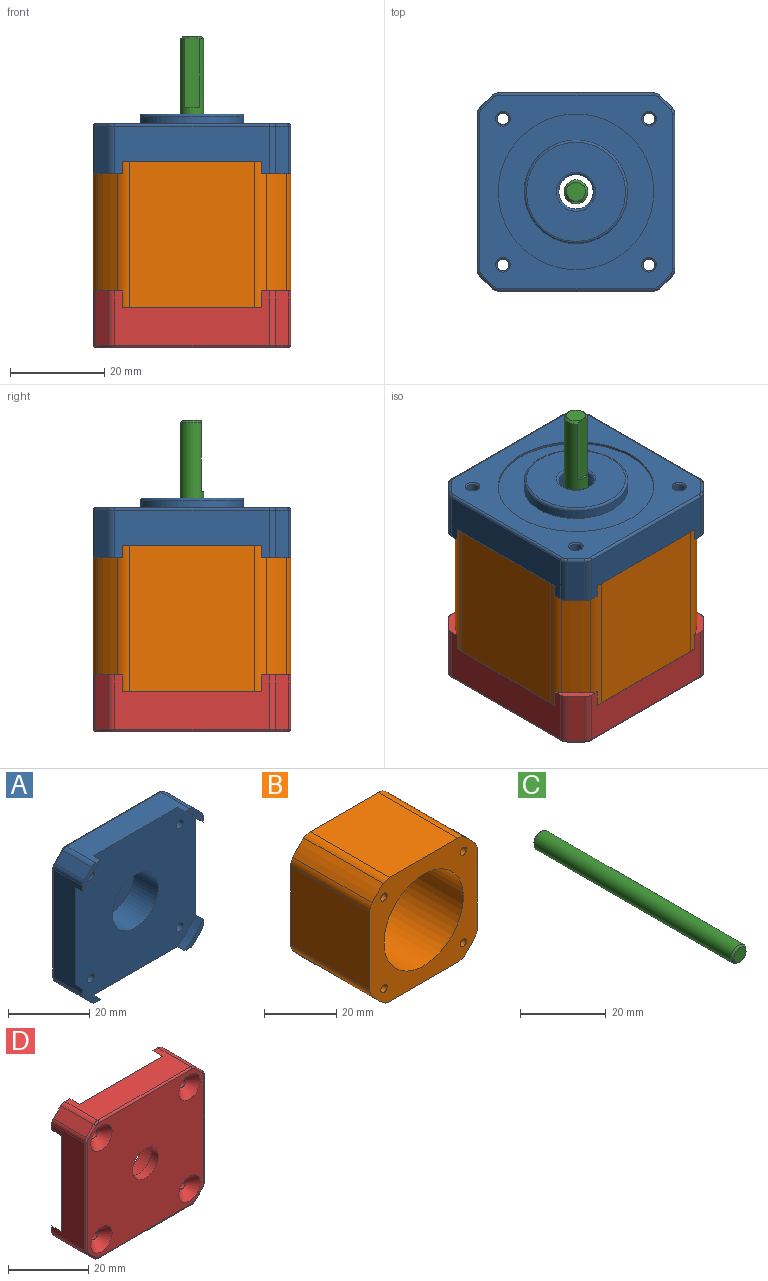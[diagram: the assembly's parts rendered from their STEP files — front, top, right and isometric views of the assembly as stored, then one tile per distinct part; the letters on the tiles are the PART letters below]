
ASSEMBLY  parts=4 mates=3
PART A: 59 faces, bbox 42.3x12.6x42.3 mm
  f0: cylinder r=3.65mm len=7.3mm, axis (0,-1,0), area 20.6mm2, adj f28,f53
  f1: plane 42x42mm, normal (0,-1,0), area 1472mm2, adj f2,f4,f6,f8,f9,f10,f11,f14
  f2: plane 32.74x10.1mm, normal (0,0,1), area 254.6mm2, adj f1,f19,f20,f21,f22,f30,f31,f51
  f3: plane 10.1x2.63mm, normal (0.71,0,0.71), area 37.5mm2, adj f22,f29,f30,f47
  f4: plane 32.74x10.1mm, normal (1,0,0), area 254.6mm2, adj f1,f21,f22,f25,f26,f29,f36,f43
  f5: plane 10.1x2.63mm, normal (0.71,0,-0.71), area 37.5mm2, adj f26,f35,f36,f39
  f6: plane 32.74x10.1mm, normal (0,0,-1), area 254.6mm2, adj f1,f23,f24,f25,f26,f34,f35,f38
  f7: plane 10.1x2.63mm, normal (-0.71,0,-0.71), area 37.5mm2, adj f24,f33,f34,f42
  f8: plane 32.74x10.1mm, normal (-1,0,0), area 254.6mm2, adj f1,f19,f20,f23,f24,f32,f33,f46
  f9: cylinder r=1.25mm len=7.7mm, axis (0,-1,0), area 60.5mm2, adj f1,f58
  f10: cylinder r=1.25mm len=7.7mm, axis (0,-1,0), area 60.5mm2, adj f1,f57
  f11: cylinder r=1.25mm len=7.7mm, axis (0,-1,0), area 60.5mm2, adj f1,f56
  f12: plane 10.1x2.63mm, normal (-0.71,0,0.71), area 37.5mm2, adj f20,f31,f32,f50
  f13: cylinder r=16.5mm len=33mm, axis (0,-1,0), area 51.8mm2, adj f15,f16
  f14: cylinder r=1.25mm len=7.7mm, axis (0,-1,0), area 60.5mm2, adj f1,f55
  f15: plane 41x41mm, normal (0,1,0), area 770.5mm2, adj f13,f37,f38,f39,f40,f41,f42,f43
  f16: plane 33x33mm, normal (0,1,0), area 475.2mm2, adj f13,f17
  f17: cylinder r=11mm len=22mm, axis (0,-1,0), area 138.2mm2, adj f16,f54
  f18: plane 21x21mm, normal (0,1,0), area 292.3mm2, adj f53,f54
  f19: cylinder r=25.6mm len=6.36mm, axis (0,1,0), area 23.5mm2, adj f1,f2,f8,f20
  f20: plane 6.36x6.36mm, normal (0,-1,0), area 10.4mm2, adj f2,f8,f12,f19,f31,f32
  f21: cylinder r=25.6mm len=6.36mm, axis (0,1,0), area 23.5mm2, adj f1,f2,f4,f22
  f22: plane 6.36x6.36mm, normal (0,-1,0), area 10.4mm2, adj f2,f3,f4,f21,f29,f30
  f23: cylinder r=25.6mm len=6.36mm, axis (0,1,0), area 23.5mm2, adj f1,f6,f8,f24
  f24: plane 6.36x6.36mm, normal (0,-1,0), area 10.4mm2, adj f6,f7,f8,f23,f33,f34
  f25: cylinder r=25.6mm len=6.36mm, axis (0,1,0), area 23.5mm2, adj f1,f4,f6,f26
  f26: plane 6.36x6.36mm, normal (0,-1,0), area 10.4mm2, adj f4,f5,f6,f25,f35,f36
  f27: cylinder r=8mm len=16mm, axis (0,-1,0), area 432.3mm2, adj f1,f28
  f28: plane 16x16mm, normal (0,-1,0), area 159.2mm2, adj f0,f27
  f29: cylinder r=2mm len=10.1mm, axis (0,-1,0), area 15.9mm2, adj f3,f4,f22,f45
  f30: cylinder r=2mm len=10.1mm, axis (0,-1,0), area 15.9mm2, adj f2,f3,f22,f49
  f31: cylinder r=2mm len=10.1mm, axis (0,-1,0), area 15.9mm2, adj f2,f12,f20,f52
  f32: cylinder r=2mm len=10.1mm, axis (0,1,0), area 15.9mm2, adj f8,f12,f20,f48
  f33: cylinder r=2mm len=10.1mm, axis (0,-1,0), area 15.9mm2, adj f7,f8,f24,f44
  f34: cylinder r=2mm len=10.1mm, axis (0,-1,0), area 15.9mm2, adj f6,f7,f24,f40
  f35: cylinder r=2mm len=10.1mm, axis (0,-1,0), area 15.9mm2, adj f5,f6,f26,f37
  f36: cylinder r=2mm len=10.1mm, axis (0,1,0), area 15.9mm2, adj f4,f5,f26,f41
  f37: torus R=1.5mm, axis (0,1,0), area 1.1mm2, adj f15,f35,f38,f39
  f38: cylinder r=0.5mm len=32.74mm, axis (1,0,0), area 25.7mm2, adj f6,f15,f37,f40
  f39: cylinder r=0.5mm len=2.98mm, axis (0.71,0,0.71), area 2.9mm2, adj f5,f15,f37,f41
  f40: torus R=1.5mm, axis (0,1,0), area 1.1mm2, adj f15,f34,f38,f42
  f41: torus R=1.5mm, axis (0,1,0), area 1.1mm2, adj f15,f36,f39,f43
  f42: cylinder r=0.5mm len=2.98mm, axis (0.71,0,-0.71), area 2.9mm2, adj f7,f15,f40,f44
  f43: cylinder r=0.5mm len=32.74mm, axis (0,0,1), area 25.7mm2, adj f4,f15,f41,f45
  f44: torus R=1.5mm, axis (0,1,0), area 1.1mm2, adj f15,f33,f42,f46
  f45: torus R=1.5mm, axis (0,1,0), area 1.1mm2, adj f15,f29,f43,f47
  f46: cylinder r=0.5mm len=32.74mm, axis (0,0,-1), area 25.7mm2, adj f8,f15,f44,f48
  f47: cylinder r=0.5mm len=2.98mm, axis (-0.71,0,0.71), area 2.9mm2, adj f3,f15,f45,f49
  f48: torus R=1.5mm, axis (0,1,0), area 1.1mm2, adj f15,f32,f46,f50
  f49: torus R=1.5mm, axis (0,1,0), area 1.1mm2, adj f15,f30,f47,f51
  f50: cylinder r=0.5mm len=2.98mm, axis (-0.71,0,-0.71), area 2.9mm2, adj f12,f15,f48,f52
  f51: cylinder r=0.5mm len=32.74mm, axis (-1,0,0), area 25.7mm2, adj f2,f15,f49,f52
  f52: torus R=1.5mm, axis (0,1,0), area 1.1mm2, adj f15,f31,f50,f51
  f53: torus R=4.15mm, axis (0,1,0), area 18.9mm2, adj f0,f18
  f54: torus R=10.5mm, axis (0,1,0), area 53.4mm2, adj f17,f18
  f55: cone r=1.25mm half-angle=45deg, axis (0,1,0), area 3.7mm2, adj f14,f15
  f56: cone r=1.25mm half-angle=45deg, axis (0,1,0), area 3.7mm2, adj f11,f15
  f57: cone r=1.25mm half-angle=45deg, axis (0,1,0), area 3.7mm2, adj f10,f15
  f58: cone r=1.25mm half-angle=45deg, axis (0,1,0), area 3.7mm2, adj f9,f15
PART B: 23 faces, bbox 42x31x42 mm
  f0: plane 42x42mm, normal (0,1,0), area 916.8mm2, adj f1,f2,f3,f4,f5,f6,f7,f8
  f1: cylinder r=25.6mm len=31mm, axis (0,-1,0), area 191.4mm2, adj f0,f16,f17,f22
  f2: plane 31x26.65mm, normal (0,0,-1), area 826.2mm2, adj f0,f15,f16,f22
  f3: cylinder r=25.6mm len=31mm, axis (0,-1,0), area 191.4mm2, adj f0,f14,f15,f22
  f4: plane 31x26.65mm, normal (-1,0,0), area 826.2mm2, adj f0,f14,f21,f22
  f5: cylinder r=25.6mm len=31mm, axis (0,-1,0), area 191.4mm2, adj f0,f20,f21,f22
  f6: plane 31x26.65mm, normal (0,0,1), area 826.2mm2, adj f0,f19,f20,f22
  f7: cylinder r=25.6mm len=31mm, axis (0,-1,0), area 191.4mm2, adj f0,f18,f19,f22
  f8: plane 31x26.65mm, normal (1,0,0), area 826.2mm2, adj f0,f17,f18,f22
  f9: cylinder r=15.5mm len=31mm, axis (0,-1,0), area 3019.1mm2, adj f0,f22
  f10: cylinder r=1.25mm len=31mm, axis (0,-1,0), area 243.5mm2, adj f0,f22
  f11: cylinder r=1.25mm len=31mm, axis (0,-1,0), area 243.5mm2, adj f0,f22
  f12: cylinder r=1.25mm len=31mm, axis (0,-1,0), area 243.5mm2, adj f0,f22
  f13: cylinder r=1.25mm len=31mm, axis (0,-1,0), area 243.5mm2, adj f0,f22
  f14: cylinder r=4mm len=31mm, axis (0,-1,0), area 82.4mm2, adj f0,f3,f4,f22
  f15: cylinder r=4mm len=31mm, axis (0,-1,0), area 82.4mm2, adj f0,f2,f3,f22
  f16: cylinder r=4mm len=31mm, axis (0,-1,0), area 82.4mm2, adj f0,f1,f2,f22
  f17: cylinder r=4mm len=31mm, axis (0,-1,0), area 82.4mm2, adj f0,f1,f8,f22
  f18: cylinder r=4mm len=31mm, axis (0,-1,0), area 82.4mm2, adj f0,f7,f8,f22
  f19: cylinder r=4mm len=31mm, axis (0,-1,0), area 82.4mm2, adj f0,f6,f7,f22
  f20: cylinder r=4mm len=31mm, axis (0,-1,0), area 82.4mm2, adj f0,f5,f6,f22
  f21: cylinder r=4mm len=31mm, axis (0,-1,0), area 82.4mm2, adj f0,f4,f5,f22
  f22: plane 42x42mm, normal (0,-1,0), area 916.8mm2, adj f1,f2,f3,f4,f5,f6,f7,f8
PART C: 7 faces, bbox 5x66x5 mm
  f0: cylinder r=2.5mm len=65mm, axis (0,-1,0), area 974.4mm2, adj f2,f3,f4,f6
  f1: plane 4x4mm, normal (0,1,0), area 12.6mm2, adj f4
  f2: plane 15x3mm, normal (0,0,-1), area 44.5mm2, adj f0,f3,f4
  f3: plane 3x0.5mm, normal (0,1,0), area 1mm2, adj f0,f2
  f4: cone r=2mm half-angle=45deg, axis (0,-1,0), area 8.6mm2, adj f0,f1,f2
  f5: plane 4x4mm, normal (0,-1,0), area 12.6mm2, adj f6
  f6: cone r=2.5mm half-angle=45deg, axis (0,1,0), area 10mm2, adj f0,f5
PART D: 53 faces, bbox 42.3x12x42.3 mm
  f0: cylinder r=4.5mm len=9mm, axis (0,-1,0), area 70.7mm2, adj f10,f28
  f1: plane 32.74x11.5mm, normal (0,0,1), area 274.1mm2, adj f9,f11,f13,f14,f16,f30,f31,f50
  f2: plane 32.74x11.5mm, normal (1,0,0), area 274.1mm2, adj f9,f11,f13,f20,f22,f29,f36,f42
  f3: plane 32.74x11.5mm, normal (0,0,-1), area 274.1mm2, adj f9,f17,f19,f20,f22,f34,f35,f39
  f4: plane 32.74x11.5mm, normal (-1,0,0), area 274.1mm2, adj f9,f14,f16,f17,f19,f32,f33,f47
  f5: cylinder r=1.25mm len=6mm, axis (0,-1,0), area 47.1mm2, adj f9,f26
  f6: cylinder r=1.25mm len=6mm, axis (0,-1,0), area 47.1mm2, adj f9,f25
  f7: cylinder r=1.25mm len=6mm, axis (0,-1,0), area 47.1mm2, adj f9,f24
  f8: cylinder r=1.25mm len=6mm, axis (0,-1,0), area 47.1mm2, adj f9,f23
  f9: plane 42x42mm, normal (0,1,0), area 1472mm2, adj f1,f2,f3,f4,f5,f6,f7,f8
  f10: plane 41x41mm, normal (0,-1,0), area 1415.7mm2, adj f0,f23,f24,f25,f26,f37,f38,f39
  f11: cylinder r=25.6mm len=6.36mm, axis (0,-1,0), area 31.6mm2, adj f1,f2,f9,f13
  f12: plane 11.5x2.63mm, normal (0.71,0,0.71), area 42.7mm2, adj f13,f29,f30,f46
  f13: plane 6.36x6.36mm, normal (0,1,0), area 10.4mm2, adj f1,f2,f11,f12,f29,f30
  f14: cylinder r=25.6mm len=6.36mm, axis (0,-1,0), area 31.6mm2, adj f1,f4,f9,f16
  f15: plane 11.5x2.63mm, normal (-0.71,0,0.71), area 42.7mm2, adj f16,f31,f32,f51
  f16: plane 6.36x6.36mm, normal (0,1,0), area 10.4mm2, adj f1,f4,f14,f15,f31,f32
  f17: cylinder r=25.6mm len=6.36mm, axis (0,-1,0), area 31.6mm2, adj f3,f4,f9,f19
  f18: plane 11.5x2.63mm, normal (-0.71,0,-0.71), area 42.7mm2, adj f19,f33,f34,f43
  f19: plane 6.36x6.36mm, normal (0,1,0), area 10.4mm2, adj f3,f4,f17,f18,f33,f34
  f20: cylinder r=25.6mm len=6.36mm, axis (0,-1,0), area 31.6mm2, adj f2,f3,f9,f22
  f21: plane 11.5x2.63mm, normal (0.71,0,-0.71), area 42.7mm2, adj f22,f35,f36,f38
  f22: plane 6.36x6.36mm, normal (0,1,0), area 10.4mm2, adj f2,f3,f20,f21,f35,f36
  f23: cone r=3.75mm half-angle=45deg, axis (0,-1,0), area 55.5mm2, adj f8,f10
  f24: cone r=3.75mm half-angle=45deg, axis (0,-1,0), area 55.5mm2, adj f7,f10
  f25: cone r=3.75mm half-angle=45deg, axis (0,-1,0), area 55.5mm2, adj f6,f10
  f26: cone r=3.75mm half-angle=45deg, axis (0,-1,0), area 55.5mm2, adj f5,f10
  f27: cylinder r=8mm len=16mm, axis (0,1,0), area 301.6mm2, adj f9,f28
  f28: plane 16x16mm, normal (0,1,0), area 137.4mm2, adj f0,f27
  f29: cylinder r=2mm len=11.5mm, axis (0,-1,0), area 18.1mm2, adj f2,f12,f13,f44
  f30: cylinder r=2mm len=11.5mm, axis (0,-1,0), area 18.1mm2, adj f1,f12,f13,f48
  f31: cylinder r=2mm len=11.5mm, axis (0,-1,0), area 18.1mm2, adj f1,f15,f16,f52
  f32: cylinder r=2mm len=11.5mm, axis (0,1,0), area 18.1mm2, adj f4,f15,f16,f49
  f33: cylinder r=2mm len=11.5mm, axis (0,-1,0), area 18.1mm2, adj f4,f18,f19,f45
  f34: cylinder r=2mm len=11.5mm, axis (0,-1,0), area 18.1mm2, adj f3,f18,f19,f41
  f35: cylinder r=2mm len=11.5mm, axis (0,-1,0), area 18.1mm2, adj f3,f21,f22,f37
  f36: cylinder r=2mm len=11.5mm, axis (0,1,0), area 18.1mm2, adj f2,f21,f22,f40
  f37: torus R=1.5mm, axis (0,1,0), area 1.1mm2, adj f10,f35,f38,f39
  f38: cylinder r=0.5mm len=2.98mm, axis (-0.71,0,-0.71), area 2.9mm2, adj f10,f21,f37,f40
  f39: cylinder r=0.5mm len=32.74mm, axis (-1,0,0), area 25.7mm2, adj f3,f10,f37,f41
  f40: torus R=1.5mm, axis (0,1,0), area 1.1mm2, adj f10,f36,f38,f42
  f41: torus R=1.5mm, axis (0,1,0), area 1.1mm2, adj f10,f34,f39,f43
  f42: cylinder r=0.5mm len=32.74mm, axis (0,0,-1), area 25.7mm2, adj f2,f10,f40,f44
  f43: cylinder r=0.5mm len=2.98mm, axis (-0.71,0,0.71), area 2.9mm2, adj f10,f18,f41,f45
  f44: torus R=1.5mm, axis (0,1,0), area 1.1mm2, adj f10,f29,f42,f46
  f45: torus R=1.5mm, axis (0,1,0), area 1.1mm2, adj f10,f33,f43,f47
  f46: cylinder r=0.5mm len=2.98mm, axis (0.71,0,-0.71), area 2.9mm2, adj f10,f12,f44,f48
  f47: cylinder r=0.5mm len=32.74mm, axis (0,0,1), area 25.7mm2, adj f4,f10,f45,f49
  f48: torus R=1.5mm, axis (0,1,0), area 1.1mm2, adj f10,f30,f46,f50
  f49: torus R=1.5mm, axis (0,1,0), area 1.1mm2, adj f10,f32,f47,f51
  f50: cylinder r=0.5mm len=32.74mm, axis (1,0,0), area 25.7mm2, adj f1,f10,f48,f52
  f51: cylinder r=0.5mm len=2.98mm, axis (0.71,0,0.71), area 2.9mm2, adj f10,f15,f49,f52
  f52: torus R=1.5mm, axis (0,1,0), area 1.1mm2, adj f10,f31,f50,f51
PLACE A rot(axis=(1,0,0),90deg) t=(0,0,39.5)mm
PLACE B rot(axis=(1,0,0),90deg) t=(0,0,23.5)mm
PLACE C rot(axis=(0,0.71,0.71),180deg) t=(0,0,0)mm
PLACE D rot(axis=(1,0,0),90deg) t=(0,0,0)mm
MATE revolute C.f0 <-> D.f0  axis (0,0,1) through (0,0,0)mm
MATE fastened A.f27 <-> B.f1  axis (0,0,-1) through (0,0,39.5)mm
MATE fastened D.f0 <-> B.f1  axis (0,0,1) through (0,0,8.5)mm
